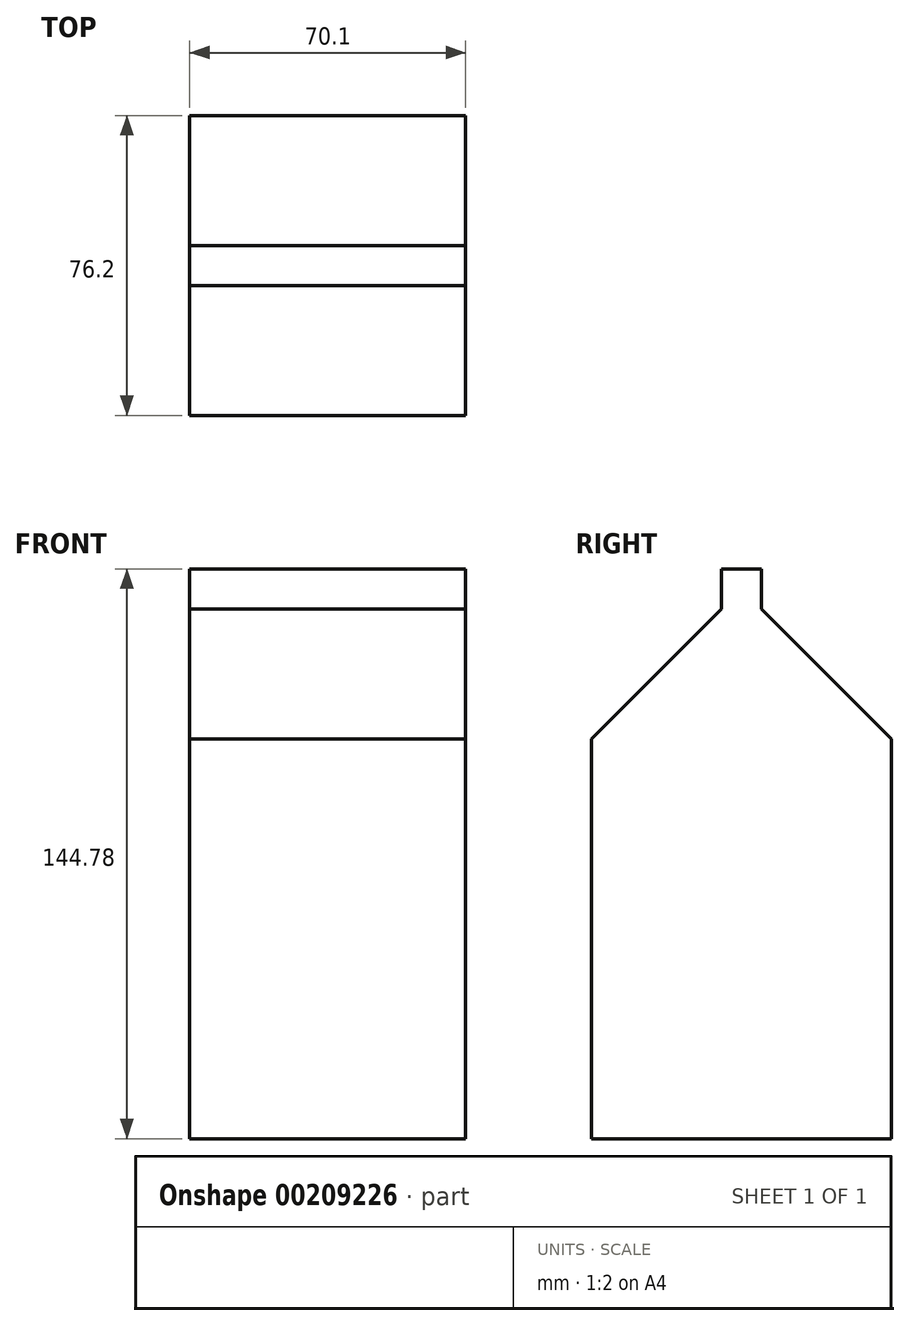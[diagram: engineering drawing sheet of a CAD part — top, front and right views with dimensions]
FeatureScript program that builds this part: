
annotation { "Feature Type Name" : "Feature", "Feature Type Description" : "" }
export const myFeature = defineFeature(function(context is Context, id is Id, definition is map)
    precondition{}
    {
        {
            var Q0;
            Q0=qCreatedBy(makeId("Right.planeOp"),FACE);
            var sketch = newSketch(context, id + "F0", { "sketchPlane" : qUnion([Q0])});
            skLineSegment(sketch, "E0.top", {"start": v(-38.1, -101.6) * mm, "end": v(38.1, -101.6) * mm});
            skLineSegment(sketch, "E0.left", {"start": v(-38.1, 0) * mm, "end": v(-38.1, -101.6) * mm});
            skLineSegment(sketch, "E0.right", {"start": v(38.1, 0) * mm, "end": v(38.1, -101.6) * mm});
            skPoint(sketch, "E0.middle", {"position": v(0, -50.8) * mm});
            skLineSegment(sketch, "E1", {"start": v(38.1, 0) * mm, "end": v(5.08, 33.02) * mm});
            skLineSegment(sketch, "E2", {"start": v(5.08, 33.02) * mm, "end": v(5.08, 43.18) * mm});
            skLineSegment(sketch, "E3", {"start": v(5.08, 43.18) * mm, "end": v(0, 43.18) * mm});
            skLineSegment(sketch, "E4.MirrorCS", {"start": v(-38.1, 0) * mm, "end": v(-5.08, 33.02) * mm});
            skLineSegment(sketch, "E5.MirrorCS", {"start": v(-5.08, 33.02) * mm, "end": v(-5.08, 43.18) * mm});
            skLineSegment(sketch, "E6.MirrorCS", {"start": v(-5.08, 43.18) * mm, "end": v(0, 43.18) * mm});
            skSolve(sketch);
        }
        {
            var Q0;
            Q0 = qSketchRegion(id + "F0", true);
            extrude(context, id + "F1", {"entities" : qUnion([Q0]), "endBound" : BoundingType.SYMMETRIC, "depth" : 70.1 * mm});
        }
    });
